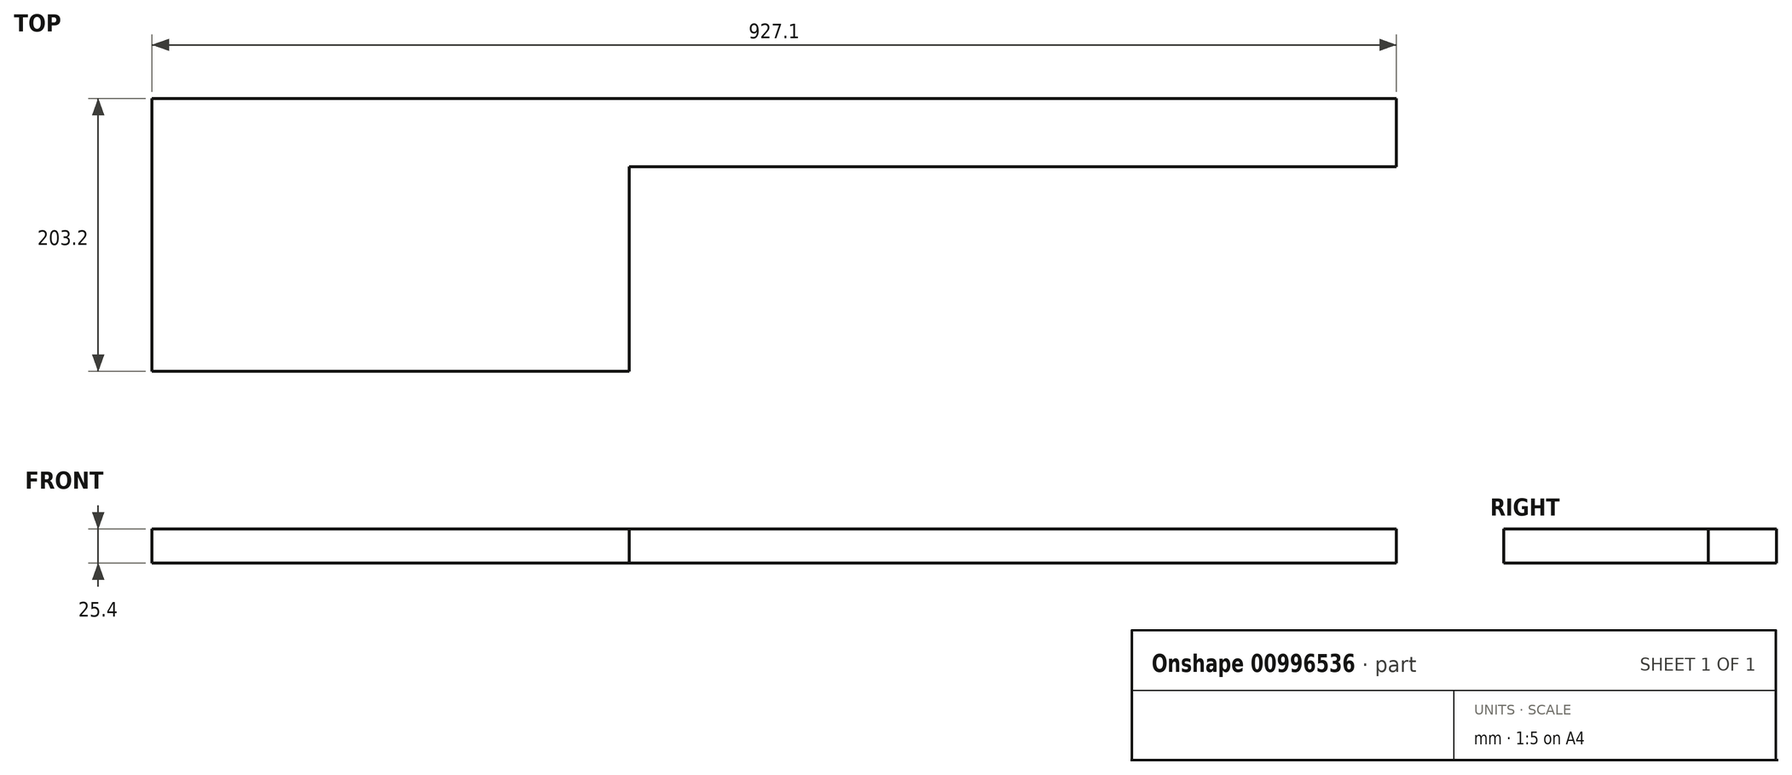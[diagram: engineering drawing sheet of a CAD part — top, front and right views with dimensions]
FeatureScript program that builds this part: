
annotation { "Feature Type Name" : "Feature", "Feature Type Description" : "" }
export const myFeature = defineFeature(function(context is Context, id is Id, definition is map)
    precondition{}
    {
        {
            var Q0;
            Q0=qCreatedBy(makeId("Top.planeOp"),FACE);
            var sketch = newSketch(context, id + "F0", { "sketchPlane" : qUnion([Q0])});
            skLineSegment(sketch, "E0.bottom", {"start": v(-134.08, 107.73) * mm, "end": v(221.52, 107.73) * mm});
            skLineSegment(sketch, "E0.top", {"start": v(-134.08, -95.47) * mm, "end": v(221.52, -95.47) * mm});
            skLineSegment(sketch, "E0.left", {"start": v(-134.08, 107.73) * mm, "end": v(-134.08, -95.47) * mm});
            skLineSegment(sketch, "E0.right", {"start": v(221.52, 107.73) * mm, "end": v(221.52, -95.47) * mm});
            skLineSegment(sketch, "E1.bottom", {"start": v(221.52, -95.47) * mm, "end": v(221.52, -95.47) * mm});
            skLineSegment(sketch, "E1.top", {"start": v(221.52, -25.62) * mm, "end": v(221.52, -25.62) * mm});
            skLineSegment(sketch, "E1.left", {"start": v(221.52, -95.47) * mm, "end": v(221.52, -25.62) * mm});
            skLineSegment(sketch, "E1.right", {"start": v(221.52, -95.47) * mm, "end": v(221.52, -25.62) * mm});
            skLineSegment(sketch, "E2.bottom", {"start": v(221.52, 107.73) * mm, "end": v(793.02, 107.73) * mm});
            skLineSegment(sketch, "E2.top", {"start": v(221.52, 56.93) * mm, "end": v(793.02, 56.93) * mm});
            skLineSegment(sketch, "E2.left", {"start": v(221.52, 107.73) * mm, "end": v(221.52, 56.93) * mm});
            skLineSegment(sketch, "E2.right", {"start": v(793.02, 107.73) * mm, "end": v(793.02, 56.93) * mm});
            skSolve(sketch);
        }
        {
            var Q0;
            Q0=makeQuery(id+"F0.imprint","IMPRINT",FACE,{"disambiguationData":[TD([[makeQuery(id+"F0.imprint","IMPRINT",EDGE,{"derivedFrom":sQuery(id+"F0.wireOp",EDGE,"E0.bottom")}),-1.0]])]});
            var Q1;
            Q1=makeQuery(id+"F0.imprint","IMPRINT",FACE,{"disambiguationData":[TD([[makeQuery(id+"F0.imprint","IMPRINT",EDGE,{"derivedFrom":sQuery(id+"F0.wireOp",EDGE,"E2.bottom")}),-1.0]])]});
            extrude(context, id + "F1", {"entities" : qUnion([Q0, Q1]), "depth" : 25.4 * mm, "offsetDistance" : 25.4 * mm});
        }
    });
